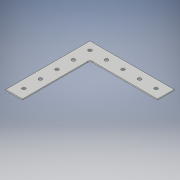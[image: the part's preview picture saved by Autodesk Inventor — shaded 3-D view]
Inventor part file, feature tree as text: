
AUTODESK INVENTOR PART (.ipt)
format: ipt  version: 2018 (Build 220112000, 112)  size: 182,784 bytes
history: native  units: in
note: dims shown in document units (in); Inventor stores cm internally (conversion verified against a paired STEP export)
features: sketch x5, extrude x4, hole x1, fillet x1
ambient origin geometry x8: Origin, YZ Plane, XZ Plane, XY Plane, X Axis, Y Axis, Z Axis, Center Point
bodies: Solid1 (feature_tree)
feature tree (11):
  extrude  "Extrusion1"  Depth=6.0in
  hole  "Hole1"  [1 undecoded]
  extrude  "Extrusion2"  Depth=0.0625in TaperAngle=0.0deg
  extrude  "Extrusion3"  Depth=1.0in
  fillet  "Fillet1"  Radius=1.0in
  extrude  "Extrusion4"  Depth=1.0in
  sketch  "Sketch1"  dims[d0=1.0in d1=6.0in]
  sketch  "Sketch2"  dims[d2=6.0in d3=1.0in]
  sketch  "Sketch3"  dims[d4=1.0in d5=0.0625in d6=0.0in]
  sketch  "Sketch4"  dims[d7=1.0in d8=1.0in d9=1.0in]
  sketch  "Sketch5"  dims[d10=1.0in d11=1.0in d12=1.0in d13=1.0in d14=1.0in d15=1.0in d16=1.0in d17=0.2in d18=0.2in d19=0.2in d20=0.2in d21=0.2in d22=0.2in d23=0.2in d24=0.2in d25=0.2in d26=0.75in d27=0.375in d28=0.25in d29=0.5635in d30=1.0in d31=0.8108in d32=0.5in d33=0.5in d34=0.0625in d35=0.0in d36=1.0in d37=0.0625in d38=0.0in d39=0.125in d40=1.0in d41=0.0in]
note: 1 required parameter value undecoded (feature->parameter linkage not recoverable at this tier; creation-order binding heuristic only, values carry confidence <= 0.55)
